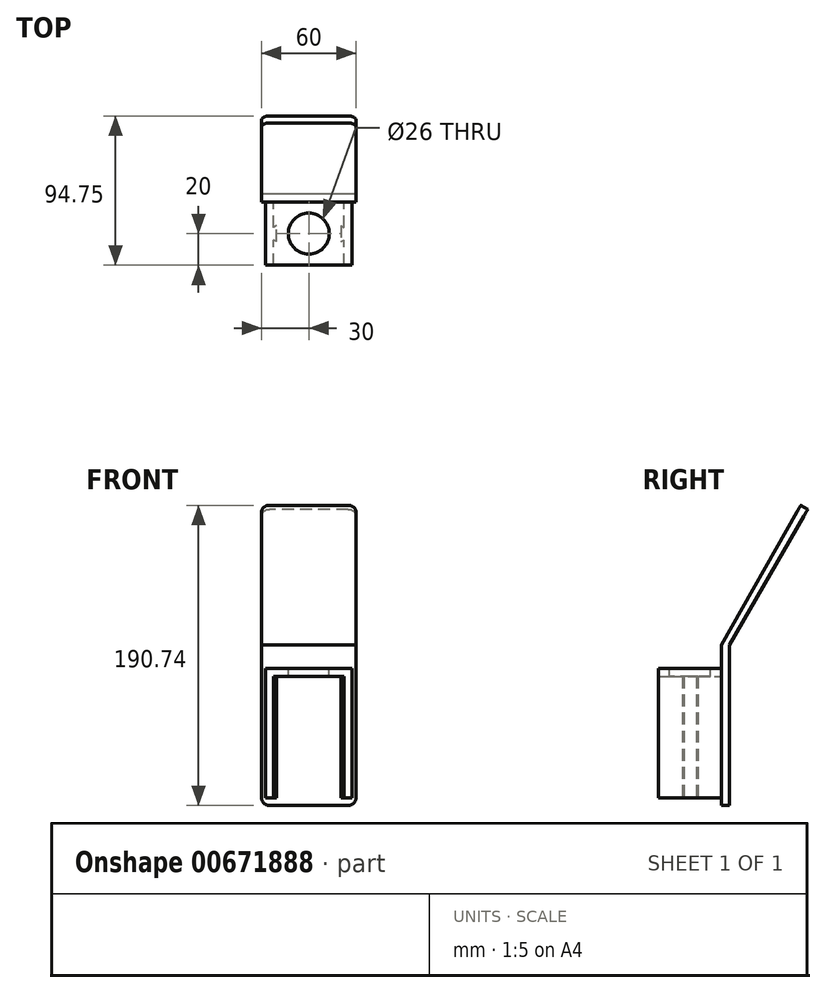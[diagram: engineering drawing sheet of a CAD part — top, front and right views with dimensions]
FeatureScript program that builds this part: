
annotation { "Feature Type Name" : "Feature", "Feature Type Description" : "" }
export const myFeature = defineFeature(function(context is Context, id is Id, definition is map)
    precondition{}
    {
        {
            var Q0;
            Q0=qCreatedBy(makeId("Right.planeOp"),FACE);
            var sketch = newSketch(context, id + "F0", { "sketchPlane" : qUnion([Q0])});
            skLineSegment(sketch, "E0.bottom", {"start": v(-2.5, 0) * mm, "end": v(2.5, 0) * mm});
            skLineSegment(sketch, "E0.top", {"start": v(-2.5, -102) * mm, "end": v(2.5, -102) * mm});
            skLineSegment(sketch, "E0.left", {"start": v(-2.5, 0) * mm, "end": v(-2.5, -102) * mm});
            skLineSegment(sketch, "E0.right", {"start": v(2.5, 0) * mm, "end": v(2.5, -102) * mm});
            skLineSegment(sketch, "E1", {"start": v(-2.5, 0) * mm, "end": v(47.79, 88.74) * mm});
            skLineSegment(sketch, "E2", {"start": v(47.79, 88.74) * mm, "end": v(52.25, 86.17) * mm});
            skLineSegment(sketch, "E3", {"start": v(52.25, 86.17) * mm, "end": v(2.5, 0) * mm});
            skSolve(sketch);
        }
        {
            var Q0;
            Q0=makeQuery(id+"F0.imprint","IMPRINT",FACE,{"disambiguationData":[TD([[makeQuery(id+"F0.imprint","IMPRINT",EDGE,{"derivedFrom":sQuery(id+"F0.wireOp",EDGE,"E0.bottom")}),1.0]])]});
            var Q1;
            Q1=makeQuery(id+"F0.imprint","IMPRINT",FACE,{"disambiguationData":[TD([[makeQuery(id+"F0.imprint","IMPRINT",EDGE,{"derivedFrom":sQuery(id+"F0.wireOp",EDGE,"E0.top")}),1.0]])]});
            extrude(context, id + "F1", {"entities" : qUnion([Q0, Q1]), "depth" : 60 * mm, "offsetDistance" : 25 * mm});
        }
        {
            var Q0;
            Q0=makeQuery(id+"F1.opExtrude","SWEPT_FACE",FACE,{"disambiguationData":[OSD([sQuery(id+"F0.wireOp",EDGE,"E0.left")])]});
            var sketch = newSketch(context, id + "F2", { "sketchPlane" : qUnion([Q0])});
            skLineSegment(sketch, "E4.bottom", {"start": v(2.5, -15) * mm, "end": v(7.5, -15) * mm});
            skLineSegment(sketch, "E4.top", {"start": v(2.5, -97) * mm, "end": v(7.5, -97) * mm});
            skLineSegment(sketch, "E4.left", {"start": v(2.5, -15) * mm, "end": v(2.5, -97) * mm});
            skLineSegment(sketch, "E4.right", {"start": v(7.5, -15) * mm, "end": v(7.5, -97) * mm});
            skLineSegment(sketch, "E5.bottom", {"start": v(52.5, -15) * mm, "end": v(57.5, -15) * mm});
            skLineSegment(sketch, "E5.top", {"start": v(52.5, -97) * mm, "end": v(57.5, -97) * mm});
            skLineSegment(sketch, "E5.left", {"start": v(52.5, -15) * mm, "end": v(52.5, -97) * mm});
            skLineSegment(sketch, "E5.right", {"start": v(57.5, -15) * mm, "end": v(57.5, -97) * mm});
            skSolve(sketch);
        }
        {
            var Q0;
            Q0=makeQuery(id+"F2.imprint","IMPRINT",FACE,{"disambiguationData":[TD([[makeQuery(id+"F2.imprint","IMPRINT",EDGE,{"derivedFrom":sQuery(id+"F2.wireOp",EDGE,"E4.bottom")}),-1.0]])]});
            var Q1;
            Q1=makeQuery(id+"F2.imprint","IMPRINT",FACE,{"disambiguationData":[TD([[makeQuery(id+"F2.imprint","IMPRINT",EDGE,{"derivedFrom":sQuery(id+"F2.wireOp",EDGE,"E5.bottom")}),-1.0]])]});
            extrude(context, id + "F3", {"entities" : qUnion([Q0, Q1]), "operationType" : NewBodyOperationType.ADD, "depth" : 40 * mm, "offsetDistance" : 25 * mm});
        }
        {
            var Q0;
            Q0=makeQuery(id+"F1.opExtrude","CAP_EDGE",EDGE,{"disambiguationData":[OSD([sQuery(id+"F0.wireOp",EDGE,"E2")])],"isStart":true});
            var Q1;
            Q1=makeQuery(id+"F1.opExtrude","CAP_EDGE",EDGE,{"disambiguationData":[OSD([sQuery(id+"F0.wireOp",EDGE,"E2")])],"isStart":false});
            var Q2;
            Q2=makeQuery(id+"F1.opExtrude","CAP_EDGE",EDGE,{"disambiguationData":[OSD([sQuery(id+"F0.wireOp",EDGE,"E0.top")])],"isStart":false});
            var Q3;
            Q3=makeQuery(id+"F1.opExtrude","CAP_EDGE",EDGE,{"disambiguationData":[OSD([sQuery(id+"F0.wireOp",EDGE,"E0.top")])],"isStart":true});
            fillet(context, id + "F4", {"entities" : qUnion([Q0, Q1, Q2, Q3]), "radius" : 5 * mm, "tangentPropagation" : true, "allowEdgeOverflow" : false});
        }
        {
            var Q0;
            Q0=makeQuery(id+"F1.opExtrude","SWEPT_FACE",FACE,{"disambiguationData":[OSD([sQuery(id+"F0.wireOp",EDGE,"E0.left")])]});
            var sketch = newSketch(context, id + "F5", { "sketchPlane" : qUnion([Q0])});
            skLineSegment(sketch, "E6.bottom", {"start": v(7.5, -15) * mm, "end": v(52.5, -15) * mm});
            skLineSegment(sketch, "E6.top", {"start": v(7.5, -20) * mm, "end": v(52.5, -20) * mm});
            skLineSegment(sketch, "E6.left", {"start": v(7.5, -15) * mm, "end": v(7.5, -20) * mm});
            skLineSegment(sketch, "E6.right", {"start": v(52.5, -15) * mm, "end": v(52.5, -20) * mm});
            skSolve(sketch);
        }
        {
            var Q0;
            Q0=makeQuery(id+"F5.imprint","IMPRINT",FACE,{"disambiguationData":[TD([[makeQuery(id+"F5.imprint","IMPRINT",EDGE,{"derivedFrom":sQuery(id+"F5.wireOp",EDGE,"E6.bottom")}),-1.0]])]});
            extrude(context, id + "F6", {"entities" : qUnion([Q0]), "operationType" : NewBodyOperationType.ADD, "depth" : 40 * mm, "offsetDistance" : 25 * mm});
        }
        {
            var Q0;
            Q0=makeQuery(id+"F6.boolean.opBoolean","MERGE",FACE,{"derivedFrom":[makeQuery(id+"F3.opExtrude","SWEPT_FACE",FACE,{"disambiguationData":[OSD([sQuery(id+"F2.wireOp",EDGE,"E4.bottom")])]}),makeQuery(id+"F3.opExtrude","SWEPT_FACE",FACE,{"disambiguationData":[OSD([sQuery(id+"F2.wireOp",EDGE,"E5.bottom")])]}),makeQuery(id+"F6.opExtrude","SWEPT_FACE",FACE,{"disambiguationData":[OSD([sQuery(id+"F5.wireOp",EDGE,"E6.bottom")])]})]});
            var sketch = newSketch(context, id + "F7", { "sketchPlane" : qUnion([Q0])});
            skLineSegment(sketch, "E7", {"start": v(30, -2.5) * mm, "end": v(30, -42.5) * mm, "construction": true});
            skLineSegment(sketch, "E8", {"start": v(2.5, -22.5) * mm, "end": v(57.5, -22.5) * mm, "construction": true});
            skCircle(sketch, "E9", {"center": v(30, -22.5) * mm, "radius": 13 * mm});
            skSolve(sketch);
        }
        {
            var Q0;
            Q0=makeQuery(id+"F7.imprint","IMPRINT",FACE,{"disambiguationData":[TD([[makeQuery(id+"F7.imprint","IMPRINT",EDGE,{"derivedFrom":sQuery(id+"F7.wireOp",EDGE,"E9")}),1.0]])]});
            extrude(context, id + "F8", {"entities" : qUnion([Q0]), "operationType" : NewBodyOperationType.REMOVE, "oppositeDirection" : true, "depth" : 25 * mm, "offsetDistance" : 25 * mm});
        }
        {
            var Q0;
            Q0=makeQuery(id+"F3.opExtrude","SWEPT_FACE",FACE,{"disambiguationData":[OSD([sQuery(id+"F2.wireOp",EDGE,"E4.top")])]});
            var sketch = newSketch(context, id + "F9", { "sketchPlane" : qUnion([Q0])});
            skLineSegment(sketch, "E10", {"start": v(2.5, 22.5) * mm, "end": v(7.5, 22.5) * mm, "construction": true});
            skLineSegment(sketch, "E11.left", {"start": v(7.5, 26.5) * mm, "end": v(7.5, 18.5) * mm});
            skLineSegment(sketch, "E11.right", {"start": v(9.5, 26.5) * mm, "end": v(9.5, 18.5) * mm});
            skLineSegment(sketch, "E12", {"start": v(9.5, 18.5) * mm, "end": v(9.5, 17.5) * mm});
            skLineSegment(sketch, "E13", {"start": v(9.5, 17.5) * mm, "end": v(7.5, 18.5) * mm});
            skLineSegment(sketch, "E14", {"start": v(9.5, 26.5) * mm, "end": v(9.5, 27.5) * mm});
            skLineSegment(sketch, "E15", {"start": v(9.5, 27.5) * mm, "end": v(7.5, 26.5) * mm});
            skSolve(sketch);
        }
        {
            var Q0;
            Q0=makeQuery(id+"F9.imprint","IMPRINT",FACE,{"disambiguationData":[TD([[makeQuery(id+"F9.imprint","IMPRINT",EDGE,{"derivedFrom":sQuery(id+"F9.wireOp",EDGE,"E11.left")}),1.0]])]});
            var Q1;
            Q1=makeQuery(id+"F6.opExtrude","SWEPT_FACE",FACE,{"disambiguationData":[OSD([sQuery(id+"F5.wireOp",EDGE,"E6.top")])]});
            extrude(context, id + "F10", {"entities" : qUnion([Q0]), "operationType" : NewBodyOperationType.ADD, "endBound" : BoundingType.UP_TO_SURFACE, "oppositeDirection" : true, "depth" : 25 * mm, "endBoundEntityFace" : qUnion([Q1]), "offsetDistance" : 25 * mm});
        }
        {
            var Q0;
            Q0=makeQuery(id+"F3.opExtrude","SWEPT_FACE",FACE,{"disambiguationData":[OSD([sQuery(id+"F2.wireOp",EDGE,"E5.top")])]});
            var sketch = newSketch(context, id + "F11", { "sketchPlane" : qUnion([Q0])});
            skLineSegment(sketch, "E16", {"start": v(57.5, 22.5) * mm, "end": v(52.5, 22.5) * mm, "construction": true});
            skLineSegment(sketch, "E17.left", {"start": v(52.5, 26.5) * mm, "end": v(52.5, 18.5) * mm});
            skLineSegment(sketch, "E17.right", {"start": v(50.5, 26.5) * mm, "end": v(50.5, 18.5) * mm});
            skLineSegment(sketch, "E18", {"start": v(50.5, 26.5) * mm, "end": v(50.5, 27.5) * mm});
            skLineSegment(sketch, "E19", {"start": v(50.5, 27.5) * mm, "end": v(52.5, 26.5) * mm});
            skLineSegment(sketch, "E20", {"start": v(50.5, 18.5) * mm, "end": v(50.5, 17.5) * mm});
            skLineSegment(sketch, "E21", {"start": v(50.5, 17.5) * mm, "end": v(52.5, 18.5) * mm});
            skSolve(sketch);
        }
        {
            var Q0;
            Q0=makeQuery(id+"F11.imprint","IMPRINT",FACE,{"disambiguationData":[TD([[makeQuery(id+"F11.imprint","IMPRINT",EDGE,{"derivedFrom":sQuery(id+"F11.wireOp",EDGE,"E17.left")}),-1.0]])]});
            var Q1;
            Q1=makeQuery(id+"F6.opExtrude","SWEPT_FACE",FACE,{"disambiguationData":[OSD([sQuery(id+"F5.wireOp",EDGE,"E6.top")])]});
            extrude(context, id + "F12", {"entities" : qUnion([Q0]), "operationType" : NewBodyOperationType.ADD, "endBound" : BoundingType.UP_TO_SURFACE, "oppositeDirection" : true, "depth" : 25 * mm, "endBoundEntityFace" : qUnion([Q1]), "offsetDistance" : 25 * mm});
        }
    });
